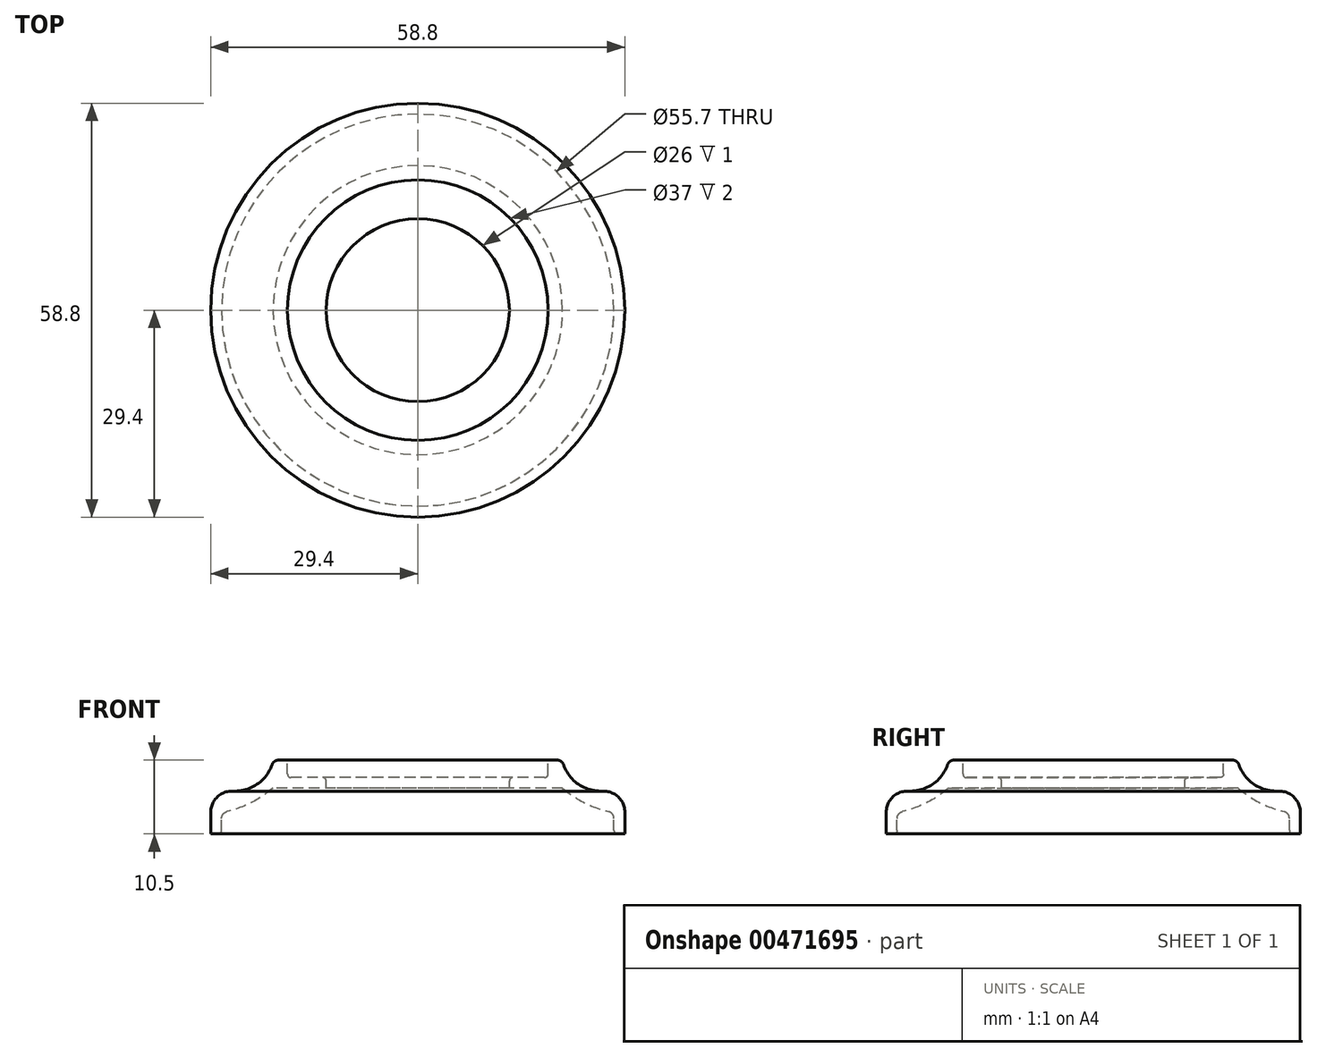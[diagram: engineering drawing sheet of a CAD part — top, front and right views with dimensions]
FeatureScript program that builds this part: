
annotation { "Feature Type Name" : "Feature", "Feature Type Description" : "" }
export const myFeature = defineFeature(function(context is Context, id is Id, definition is map)
    precondition{}
    {
        {
            var Q0;
            Q0=qCreatedBy(makeId("Front.planeOp"),FACE);
            var sketch = newSketch(context, id + "F0", { "sketchPlane" : qUnion([Q0])});
            skLineSegment(sketch, "E0", {"start": v(0, 40.1) * mm, "end": v(0, 0) * mm, "construction": true});
            skLineSegment(sketch, "E1", {"start": v(0, 0) * mm, "end": v(-34.34, 0) * mm, "construction": true});
            skLineSegment(sketch, "E2", {"start": v(-13.5, 23.69) * mm, "end": v(-18, 23.69) * mm});
            skLineSegment(sketch, "E3", {"start": v(-18.5, 24.19) * mm, "end": v(-18.5, 26.19) * mm});
            skLineSegment(sketch, "E4", {"start": v(-18.5, 26.19) * mm, "end": v(-19.74, 26.19) * mm});
            skLineSegment(sketch, "E5", {"start": v(-29.4, 18.76) * mm, "end": v(-29.4, 15.69) * mm});
            skLineSegment(sketch, "E6", {"start": v(-13, 23.19) * mm, "end": v(-13, 22.19) * mm});
            skLineSegment(sketch, "E7", {"start": v(-13, 22.19) * mm, "end": v(-20.54, 22.19) * mm});
            skLineSegment(sketch, "E8", {"start": v(-29.4, 15.69) * mm, "end": v(-27.85, 15.69) * mm});
            skLineSegment(sketch, "E9", {"start": v(-27.85, 15.69) * mm, "end": v(-27.85, 17.88) * mm});
            skArc(sketch, "E10", {"start": v(-27.09, 18.85) * mm, "mid": v(-23.62, 20.14) * mm, "end": v(-20.54, 22.19) * mm});
            skPoint(sketch, "E11.visualSharp", {"position": v(-20.5, 21.76) * mm});
            skArc(sketch, "E12", {"start": v(-26.01, 21.76) * mm, "mid": v(-22.75, 22.78) * mm, "end": v(-20.69, 25.51) * mm});
            skPoint(sketch, "E13.visualSharp", {"position": v(-29.4, 21.76) * mm});
            skArc(sketch, "E13.filletArc", {"start": v(-26.4, 21.76) * mm, "mid": v(-28.52, 20.88) * mm, "end": v(-29.4, 18.76) * mm});
            skLineSegment(sketch, "E14.trimOffspring", {"start": v(-25.9, 21.76) * mm, "end": v(-26.4, 21.76) * mm});
            skPoint(sketch, "E15.visualSharp", {"position": v(-27.85, 18.69) * mm});
            skArc(sketch, "E15.filletArc", {"start": v(-27.09, 18.85) * mm, "mid": v(-27.64, 18.5) * mm, "end": v(-27.85, 17.88) * mm});
            skPoint(sketch, "E16.visualSharp", {"position": v(-20.5, 26.19) * mm});
            skArc(sketch, "E16.filletArc", {"start": v(-19.74, 26.19) * mm, "mid": v(-20.32, 26) * mm, "end": v(-20.69, 25.51) * mm});
            skPoint(sketch, "E17.visualSharp", {"position": v(-18.5, 23.69) * mm});
            skArc(sketch, "E17.filletArc", {"start": v(-18.5, 24.19) * mm, "mid": v(-18.35, 23.83) * mm, "end": v(-18, 23.69) * mm});
            skPoint(sketch, "E18.visualSharp", {"position": v(-13, 23.69) * mm});
            skArc(sketch, "E18.filletArc", {"start": v(-13, 23.19) * mm, "mid": v(-13.15, 23.54) * mm, "end": v(-13.5, 23.69) * mm});
            skSolve(sketch);
        }
        {
            var Q0;
            Q0 = qSketchRegion(id + "F0", true);
            var Q1;
            Q1=sQuery(id+"F0.wireOp",EDGE,"E0");
            revolve(context, id + "F1", {"entities" : qUnion([Q0]), "axis" : qUnion([Q1]), "revolveType" : RevolveType.FULL});
        }
        {
            var Q0;
            Q0=makeQuery(id+"F1.opRevolve","SWEPT_EDGE",EDGE,{"disambiguationData":[OSD([sQuery(id+"F0.wireOp",EDGE,"E8"),sQuery(id+"F0.wireOp",EDGE,"E9")])]});
            fillet(context, id + "F2", {"entities" : qUnion([Q0]), "radius" : .5 * mm, "tangentPropagation" : true, "allowEdgeOverflow" : false});
        }
    });
